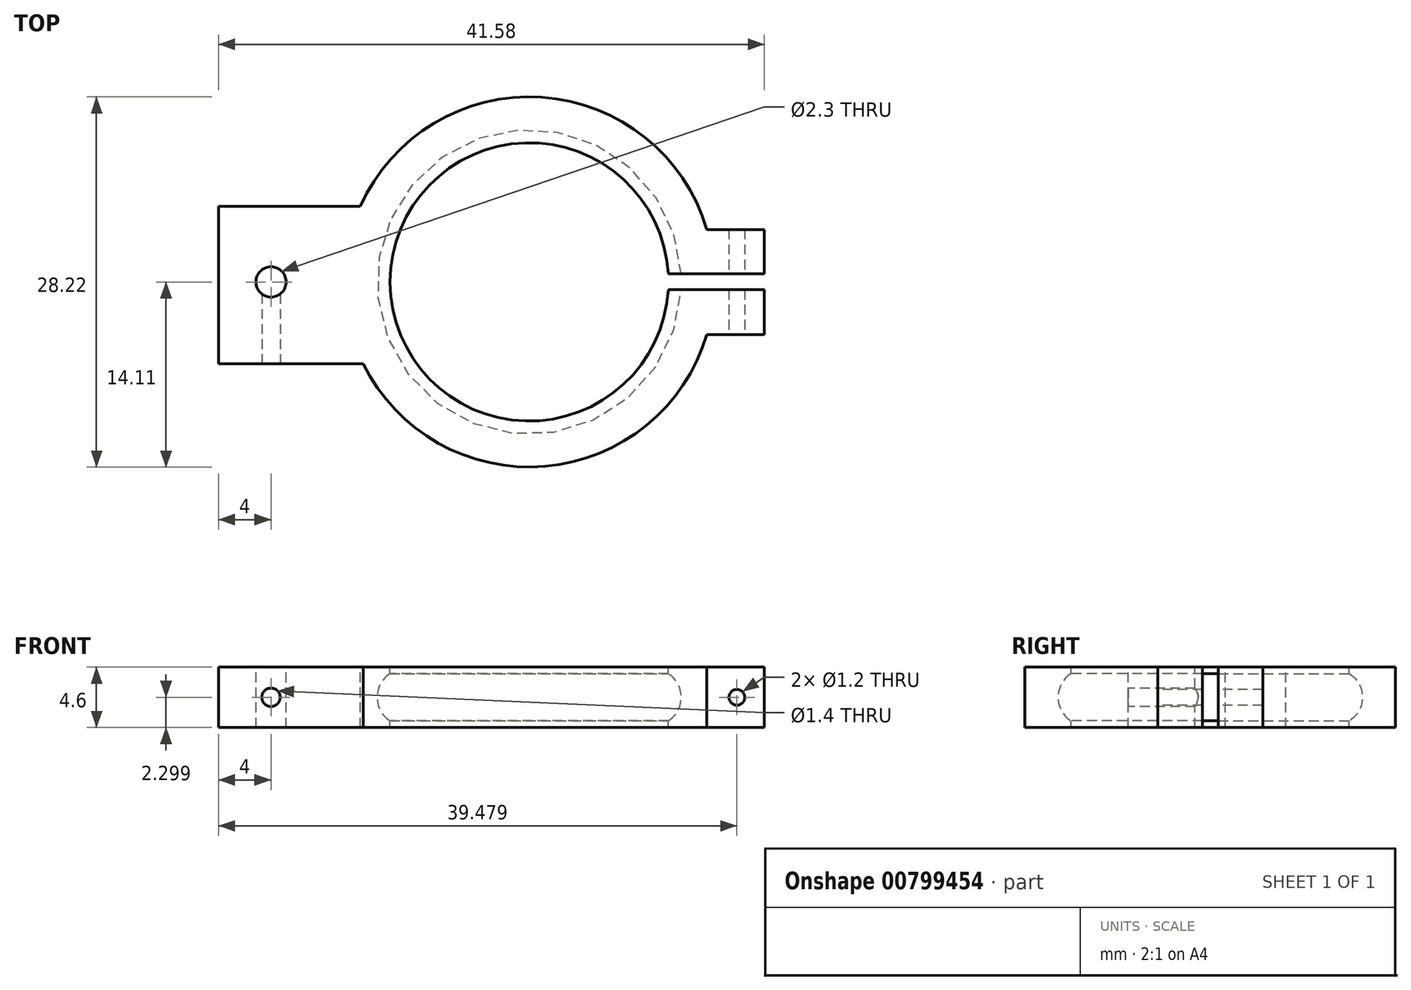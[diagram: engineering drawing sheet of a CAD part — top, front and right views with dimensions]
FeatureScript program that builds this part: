
annotation { "Feature Type Name" : "Feature", "Feature Type Description" : "" }
export const myFeature = defineFeature(function(context is Context, id is Id, definition is map)
    precondition{}
    {
        {
            var Q0;
            Q0=qCreatedBy(makeId("Front.planeOp"),FACE);
            var sketch = newSketch(context, id + "F0", { "sketchPlane" : qUnion([Q0])});
            skCircle(sketch, "E0", {"center": v(-10.93, 4.35) * mm, "radius": 2.3 * mm});
            skLineSegment(sketch, "E1", {"start": v(-0.33, 7.42) * mm, "end": v(-0.33, 0.75) * mm});
            skArc(sketch, "E2", {"start": v(-10.93, 6.65) * mm, "mid": v(-13.23, 4.35) * mm, "end": v(-10.93, 2.05) * mm});
            skLineSegment(sketch, "E3", {"start": v(-10.93, 6.65) * mm, "end": v(-10.93, 2.05) * mm});
            skLineSegment(sketch, "E4", {"start": v(-10.93, 6.15) * mm, "end": v(-12.36, 6.15) * mm});
            skLineSegment(sketch, "E5", {"start": v(-10.93, 2.55) * mm, "end": v(-12.36, 2.55) * mm});
            skLineSegment(sketch, "E6", {"start": v(-10.93, 6.65) * mm, "end": v(-14.43, 6.65) * mm});
            skLineSegment(sketch, "E7", {"start": v(-14.43, 6.65) * mm, "end": v(-14.43, 2.05) * mm});
            skLineSegment(sketch, "E8", {"start": v(-14.43, 2.05) * mm, "end": v(-10.93, 2.05) * mm});
            skLineSegment(sketch, "E9", {"start": v(-11.93, 5.53) * mm, "end": v(-11.93, 3.18) * mm});
            skArc(sketch, "E10", {"start": v(-10.93, 6.15) * mm, "mid": v(-11.92, 4.35) * mm, "end": v(-10.93, 2.55) * mm});
            skSolve(sketch);
        }
        {
            var Q0;
            {var subQ3=sQuery(id+"F0.wireOp",EDGE,"E4");Q0=makeQuery(id+"F0.imprint","IMPRINT",FACE,{"disambiguationData":[TD([[makeQuery(id+"F0.imprint","IMPRINT",EDGE,{"derivedFrom":subQ3}),-1.0]])]});}
            var Q1;
            {var subQ0=sQuery(id+"F0.wireOp",EDGE,"E6");Q1=makeQuery(id+"F0.imprint","IMPRINT",FACE,{"disambiguationData":[TD([[makeQuery(id+"F0.imprint","IMPRINT",EDGE,{"derivedFrom":subQ0}),1.0]])]});}
            var Q2;
            {var subQ0=sQuery(id+"F0.wireOp",EDGE,"E4");Q2=makeQuery(id+"F0.imprint","IMPRINT",FACE,{"disambiguationData":[TD([[makeQuery(id+"F0.imprint","IMPRINT",EDGE,{"derivedFrom":subQ0}),1.0]])]});}
            var Q3;
            {var subQ3=sQuery(id+"F0.wireOp",EDGE,"E5");Q3=makeQuery(id+"F0.imprint","IMPRINT",FACE,{"disambiguationData":[TD([[makeQuery(id+"F0.imprint","IMPRINT",EDGE,{"derivedFrom":subQ3}),1.0]])]});}
            var Q4;
            Q4=sQuery(id+"F0.wireOp",EDGE,"E1");
            revolve(context, id + "F1", {"surfaceOperationType" : NewSurfaceOperationType.NEW, "entities" : qUnion([Q0, Q1, Q2, Q3]), "axis" : qUnion([Q4]), "revolveType" : RevolveType.FULL});
        }
        {
            var Q0;
            Q0=makeQuery(id+"F1.opRevolve","SWEPT_FACE",FACE,{"disambiguationData":[OSD([sQuery(id+"F0.wireOp",EDGE,"E6")])]});
            var sketch = newSketch(context, id + "F2", { "sketchPlane" : qUnion([Q0])});
            skLineSegment(sketch, "E11.bottom", {"start": v(11.8, 4) * mm, "end": v(17.58, 4) * mm});
            skLineSegment(sketch, "E11.top", {"start": v(11.8, -4) * mm, "end": v(17.58, -4) * mm});
            skLineSegment(sketch, "E11.left", {"start": v(11.8, 4) * mm, "end": v(11.8, -4) * mm});
            skLineSegment(sketch, "E11.right", {"start": v(17.58, 4) * mm, "end": v(17.58, -4) * mm});
            skLineSegment(sketch, "E12", {"start": v(11.8, 0.61) * mm, "end": v(17.58, 0.61) * mm});
            skLineSegment(sketch, "E13", {"start": v(11.8, -0.59) * mm, "end": v(17.58, -0.59) * mm});
            skLineSegment(sketch, "E14.bottom", {"start": v(-12.37, 5.76) * mm, "end": v(-24, 5.76) * mm});
            skLineSegment(sketch, "E14.top", {"start": v(-12.37, -6.24) * mm, "end": v(-24, -6.24) * mm});
            skLineSegment(sketch, "E14.left", {"start": v(-12.37, 5.76) * mm, "end": v(-12.37, -6.24) * mm});
            skLineSegment(sketch, "E14.right", {"start": v(-24, 5.76) * mm, "end": v(-24, -6.24) * mm});
            skPoint(sketch, "E15", {"position": v(0, 0) * mm});
            skCircle(sketch, "E16", {"center": v(-20, 0) * mm, "radius": 1.15 * mm});
            skSolve(sketch);
        }
        {
            var Q0;
            {var subQ0=sQuery(id+"F2.wireOp",EDGE,"E14.right");Q0=makeQuery(id+"F2.imprint","IMPRINT",FACE,{"disambiguationData":[TD([[makeQuery(id+"F2.imprint","IMPRINT",EDGE,{"derivedFrom":subQ0}),1.0]])]});}
            var Q1;
            {var subQ0=sQuery(id+"F2.wireOp",EDGE,"E11.right");var subQ1=sQuery(id+"F2.wireOp",EDGE,"E11.bottom");var subQ2=makeQuery(id+"F2.imprint","INTERSECT",VERTEX,{"derivedFrom":[subQ1,subQ0]});Q1=makeQuery(id+"F2.imprint","IMPRINT",FACE,{"disambiguationData":[TD([[makeQuery(id+"F2.imprint","IMPRINT",EDGE,{"disambiguationData":[TD([[subQ2,-1.0]])],"derivedFrom":subQ0}),-1.0]])]});}
            var Q2;
            {var subQ0=sQuery(id+"F2.wireOp",EDGE,"E11.right");var subQ1=sQuery(id+"F2.wireOp",EDGE,"E11.top");var subQ2=makeQuery(id+"F2.imprint","INTERSECT",VERTEX,{"derivedFrom":[subQ1,subQ0]});Q2=makeQuery(id+"F2.imprint","IMPRINT",FACE,{"disambiguationData":[TD([[makeQuery(id+"F2.imprint","IMPRINT",EDGE,{"disambiguationData":[TD([[subQ2,1.0]])],"derivedFrom":subQ0}),-1.0]])]});}
            var Q3;
            {var subQ0=sQuery(id+"F2.wireOp",EDGE,"E11.left");var subQ1=sQuery(id+"F2.wireOp",EDGE,"E11.bottom");var subQ2=makeQuery(id+"F2.imprint","INTERSECT",VERTEX,{"derivedFrom":[subQ1,subQ0]});Q3=makeQuery(id+"F2.imprint","IMPRINT",FACE,{"disambiguationData":[TD([[makeQuery(id+"F2.imprint","IMPRINT",EDGE,{"disambiguationData":[TD([[subQ2,-1.0]])],"derivedFrom":subQ0}),1.0]])]});}
            var Q4;
            {var subQ0=sQuery(id+"F2.wireOp",EDGE,"E11.left");var subQ1=sQuery(id+"F2.wireOp",EDGE,"E11.top");var subQ2=makeQuery(id+"F2.imprint","INTERSECT",VERTEX,{"derivedFrom":[subQ1,subQ0]});Q4=makeQuery(id+"F2.imprint","IMPRINT",FACE,{"disambiguationData":[TD([[makeQuery(id+"F2.imprint","IMPRINT",EDGE,{"disambiguationData":[TD([[subQ2,1.0]])],"derivedFrom":subQ0}),1.0]])]});}
            var Q5;
            {var subQ0=sQuery(id+"F2.wireOp",EDGE,"E14.left");Q5=makeQuery(id+"F2.imprint","IMPRINT",FACE,{"disambiguationData":[TD([[makeQuery(id+"F2.imprint","IMPRINT",EDGE,{"derivedFrom":subQ0}),-1.0]])]});}
            extrude(context, id + "F3", {"entities" : qUnion([Q0, Q1, Q2, Q3, Q4, Q5]), "operationType" : NewBodyOperationType.ADD, "oppositeDirection" : true, "depth" : 4.6 * mm, "offsetDistance" : 25 * mm});
        }
        {
            var Q0;
            Q0=makeQuery(id+"F3.opExtrude","SWEPT_FACE",FACE,{"disambiguationData":[OSD([sQuery(id+"F2.wireOp",EDGE,"E14.top")])]});
            var sketch = newSketch(context, id + "F4", { "sketchPlane" : qUnion([Q0])});
            skCircle(sketch, "E17", {"center": v(-20, 4.35) * mm, "radius": 0.7 * mm});
            skPoint(sketch, "E17.centerSnap0", {"position": v(-24, 4.35) * mm});
            skSolve(sketch);
        }
        {
            var Q0;
            Q0=makeQuery(id+"F4.imprint","IMPRINT",FACE,{"disambiguationData":[TD([[makeQuery(id+"F4.imprint","IMPRINT",EDGE,{"derivedFrom":sQuery(id+"F4.wireOp",EDGE,"E17")}),1.0]])]});
            extrude(context, id + "F5", {"entities" : qUnion([Q0]), "operationType" : NewBodyOperationType.REMOVE, "oppositeDirection" : true, "depth" : 6 * mm, "offsetDistance" : 25 * mm});
        }
        {
            var Q0;
            Q0=makeQuery(id+"F3.opExtrude","SWEPT_FACE",FACE,{"disambiguationData":[OSD([sQuery(id+"F2.wireOp",EDGE,"E11.top")])]});
            var sketch = newSketch(context, id + "F6", { "sketchPlane" : qUnion([Q0])});
            skCircle(sketch, "E18", {"center": v(15.48, 4.35) * mm, "radius": 0.6 * mm});
            skPoint(sketch, "E18.centerSnap0", {"position": v(17.58, 4.35) * mm});
            skSolve(sketch);
        }
        {
            var Q0;
            Q0=makeQuery(id+"F6.imprint","IMPRINT",FACE,{"disambiguationData":[TD([[makeQuery(id+"F6.imprint","IMPRINT",EDGE,{"derivedFrom":sQuery(id+"F6.wireOp",EDGE,"E18")}),1.0]])]});
            extrude(context, id + "F7", {"entities" : qUnion([Q0]), "operationType" : NewBodyOperationType.REMOVE, "oppositeDirection" : true, "depth" : 25 * mm, "offsetDistance" : 25 * mm});
        }
        {
            var Q0;
            {var subQ0=sQuery(id+"F2.wireOp",EDGE,"E11.right");var subQ1=sQuery(id+"F2.wireOp",EDGE,"E11.left");Q0=makeQuery(id+"F3.boolean.opBoolean","MERGE",FACE,{"derivedFrom":[makeQuery(id+"F1.opRevolve","SWEPT_FACE",FACE,{"disambiguationData":[OSD([sQuery(id+"F0.wireOp",EDGE,"E6")])]}),makeQuery(id+"F3.opExtrude","CAP_FACE",FACE,{"disambiguationData":[OSD([sQuery(id+"F2.wireOp",EDGE,"E11.bottom"),subQ1,subQ0,sQuery(id+"F2.wireOp",EDGE,"E12")])],"isStart":true}),makeQuery(id+"F3.opExtrude","CAP_FACE",FACE,{"disambiguationData":[OSD([sQuery(id+"F2.wireOp",EDGE,"E11.top"),subQ1,subQ0,sQuery(id+"F2.wireOp",EDGE,"E13")])],"isStart":true}),makeQuery(id+"F3.opExtrude","CAP_FACE",FACE,{"disambiguationData":[OSD([sQuery(id+"F2.wireOp",EDGE,"E14.bottom"),sQuery(id+"F2.wireOp",EDGE,"E14.top"),sQuery(id+"F2.wireOp",EDGE,"E14.left"),sQuery(id+"F2.wireOp",EDGE,"E14.right"),sQuery(id+"F2.wireOp",EDGE,"E16")])],"isStart":true})]});}
            var sketch = newSketch(context, id + "F8", { "sketchPlane" : qUnion([Q0])});
            skLineSegment(sketch, "E19.bottom", {"start": v(14.34, 0.61) * mm, "end": v(8.9, 0.61) * mm});
            skLineSegment(sketch, "E19.top", {"start": v(14.34, -0.59) * mm, "end": v(8.9, -0.59) * mm});
            skLineSegment(sketch, "E19.left", {"start": v(14.34, 0.61) * mm, "end": v(14.34, -0.59) * mm});
            skLineSegment(sketch, "E19.right", {"start": v(8.9, 0.61) * mm, "end": v(8.9, -0.59) * mm});
            skSolve(sketch);
        }
        {
            var Q0;
            {var subQ0=sQuery(id+"F8.wireOp",EDGE,"E19.right");Q0=makeQuery(id+"F8.imprint","IMPRINT",FACE,{"disambiguationData":[TD([[makeQuery(id+"F8.imprint","IMPRINT",EDGE,{"derivedFrom":subQ0}),1.0]])]});}
            var Q1;
            {var subQ0=sQuery(id+"F8.wireOp",EDGE,"E19.bottom");var subQ4=sQuery(id+"F0.wireOp",EDGE,"E6");var subQ8=makeQuery(id+"F1.opRevolve","SWEPT_EDGE",EDGE,{"disambiguationData":[OSD([sQuery(id+"F0.wireOp",EDGE,"E0"),sQuery(id+"F0.wireOp",EDGE,"E3"),subQ4])]});var subQ9=makeQuery(id+"F8.imprint","INTERSECT",VERTEX,{"derivedFrom":[subQ8,subQ0]});Q1=makeQuery(id+"F8.imprint","IMPRINT",FACE,{"disambiguationData":[TD([[makeQuery(id+"F8.imprint","IMPRINT",EDGE,{"disambiguationData":[TD([[subQ9,1.0]])],"derivedFrom":subQ8}),-1.0]])]});}
            var Q2;
            {var subQ8=sQuery(id+"F8.wireOp",EDGE,"E19.left");Q2=makeQuery(id+"F8.imprint","IMPRINT",FACE,{"disambiguationData":[TD([[makeQuery(id+"F8.imprint","IMPRINT",EDGE,{"derivedFrom":subQ8}),-1.0]])]});}
            extrude(context, id + "F9", {"entities" : qUnion([Q0, Q1, Q2]), "operationType" : NewBodyOperationType.REMOVE, "oppositeDirection" : true, "depth" : 25 * mm, "offsetDistance" : 25 * mm});
        }
    });
